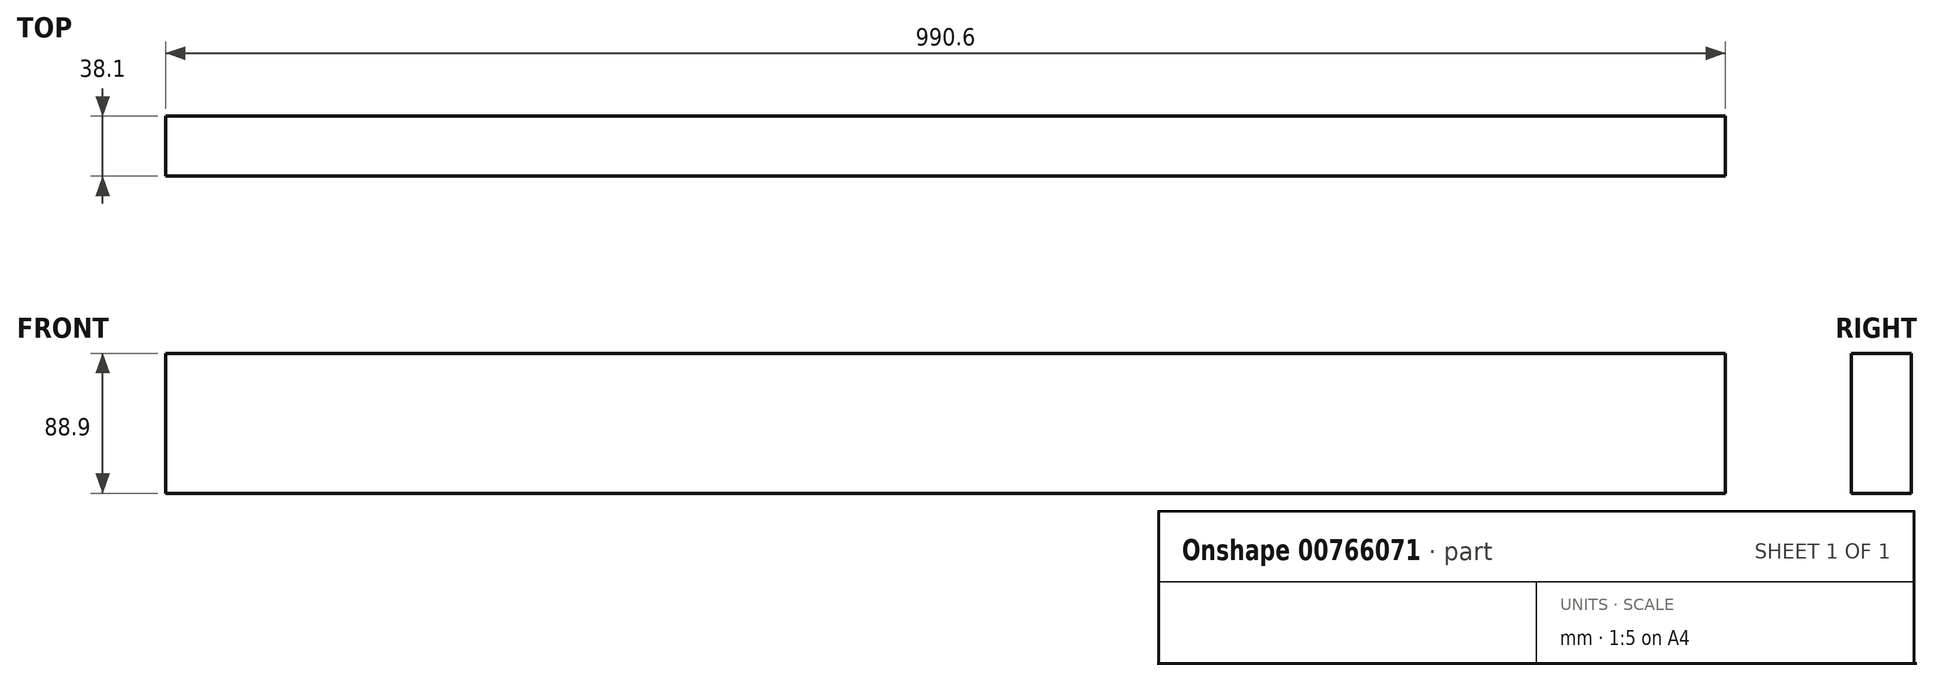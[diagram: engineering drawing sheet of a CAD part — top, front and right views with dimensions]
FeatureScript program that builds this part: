
annotation { "Feature Type Name" : "Feature", "Feature Type Description" : "" }
export const myFeature = defineFeature(function(context is Context, id is Id, definition is map)
    precondition{}
    {
        {
            var Q0;
            Q0=qCreatedBy(makeId("Front.planeOp"),FACE);
            var sketch = newSketch(context, id + "F0", { "sketchPlane" : qUnion([Q0])});
            skLineSegment(sketch, "E0.bottom", {"start": v(-447.7, 33.68) * mm, "end": v(542.9, 33.68) * mm});
            skLineSegment(sketch, "E0.top", {"start": v(-447.7, -55.22) * mm, "end": v(542.9, -55.22) * mm});
            skLineSegment(sketch, "E0.left", {"start": v(-447.7, 33.68) * mm, "end": v(-447.7, -55.22) * mm});
            skLineSegment(sketch, "E0.right", {"start": v(542.9, 33.68) * mm, "end": v(542.9, -55.22) * mm});
            skSolve(sketch);
        }
        {
            var Q0;
            Q0=qSketchRegion(id+"F0",true);
            extrude(context, id + "F1", {"entities" : qUnion([Q0]), "depth" : 38.1 * mm, "offsetDistance" : 25.4 * mm});
        }
    });
